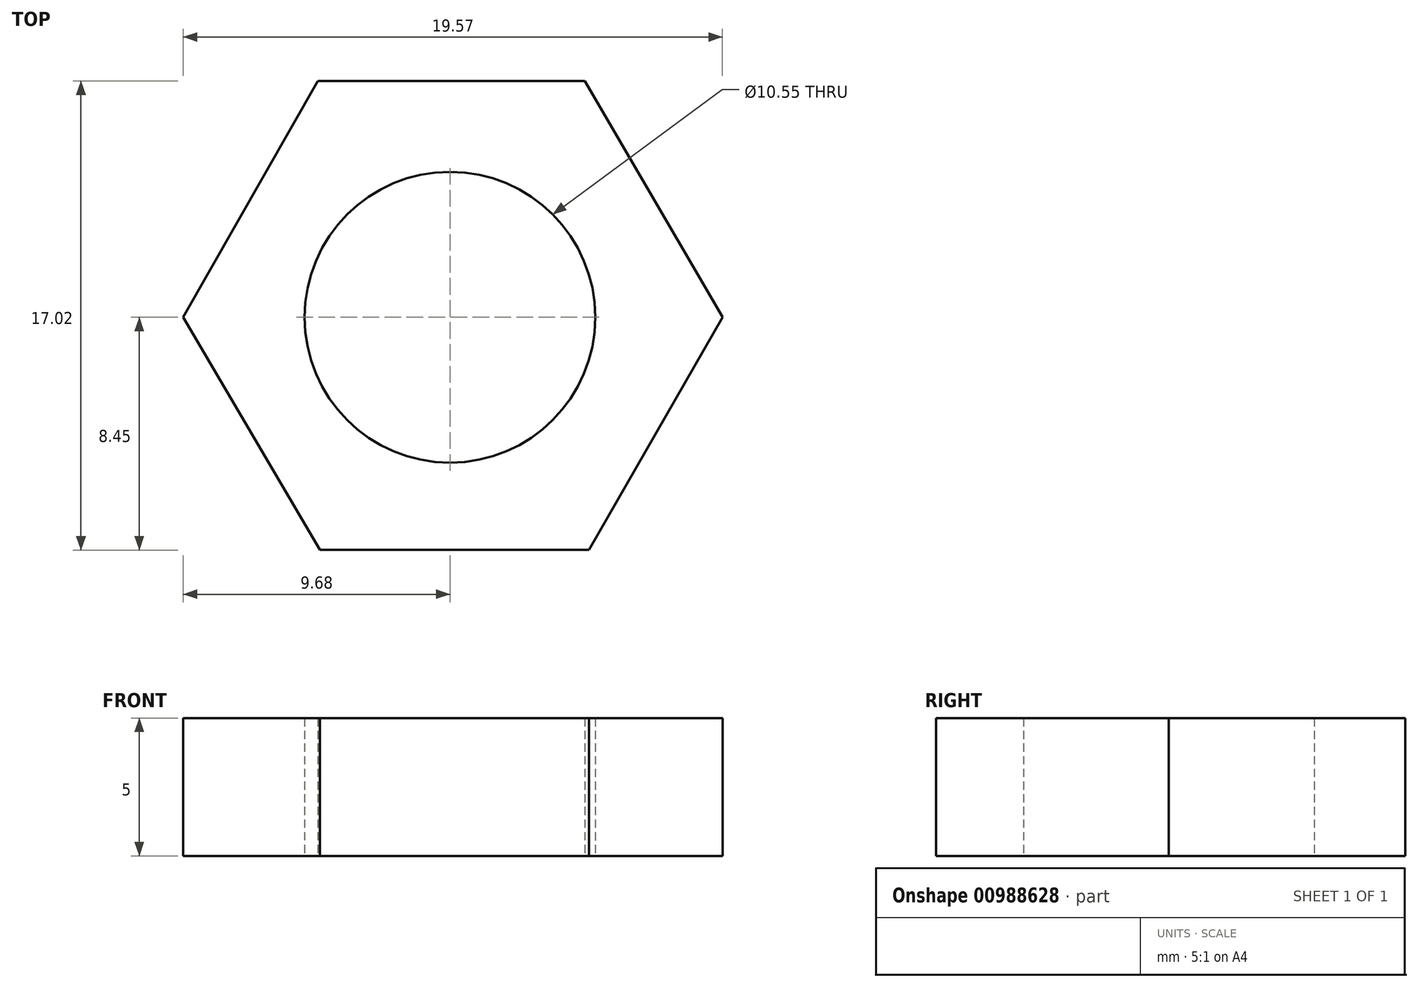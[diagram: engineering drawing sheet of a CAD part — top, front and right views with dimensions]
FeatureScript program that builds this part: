
annotation { "Feature Type Name" : "Feature", "Feature Type Description" : "" }
export const myFeature = defineFeature(function(context is Context, id is Id, definition is map)
    precondition{}
    {
        {
            var Q0;
            Q0=qCreatedBy(makeId("Top.planeOp"),FACE);
            var sketch = newSketch(context, id + "F0", { "sketchPlane" : qUnion([Q0])});
            skCircle(sketch, "E0", {"center": v(0, 0) * mm, "radius": 5.28 * mm});
            skLineSegment(sketch, "E1", {"start": v(-4.8, 8.57) * mm, "end": v(4.9, 8.57) * mm});
            skLineSegment(sketch, "E2", {"start": v(4.9, 8.57) * mm, "end": v(9.9, 0) * mm});
            skLineSegment(sketch, "E3", {"start": v(9.9, 0) * mm, "end": v(5.05, -8.45) * mm});
            skLineSegment(sketch, "E4", {"start": v(5.05, -8.45) * mm, "end": v(-4.72, -8.45) * mm});
            skLineSegment(sketch, "E5", {"start": v(-4.72, -8.45) * mm, "end": v(-9.68, 0) * mm});
            skLineSegment(sketch, "E6", {"start": v(-9.68, 0) * mm, "end": v(-4.8, 8.57) * mm});
            skSolve(sketch);
        }
        {
            var Q0;
            Q0=makeQuery(id+"F0.imprint","IMPRINT",FACE,{"disambiguationData":[TD([[makeQuery(id+"F0.imprint","IMPRINT",EDGE,{"derivedFrom":sQuery(id+"F0.wireOp",EDGE,"E0")}),-1.0]])]});
            extrude(context, id + "F1", {"entities" : qUnion([Q0]), "depth" : 5 * mm, "offsetDistance" : 25 * mm});
        }
    });
